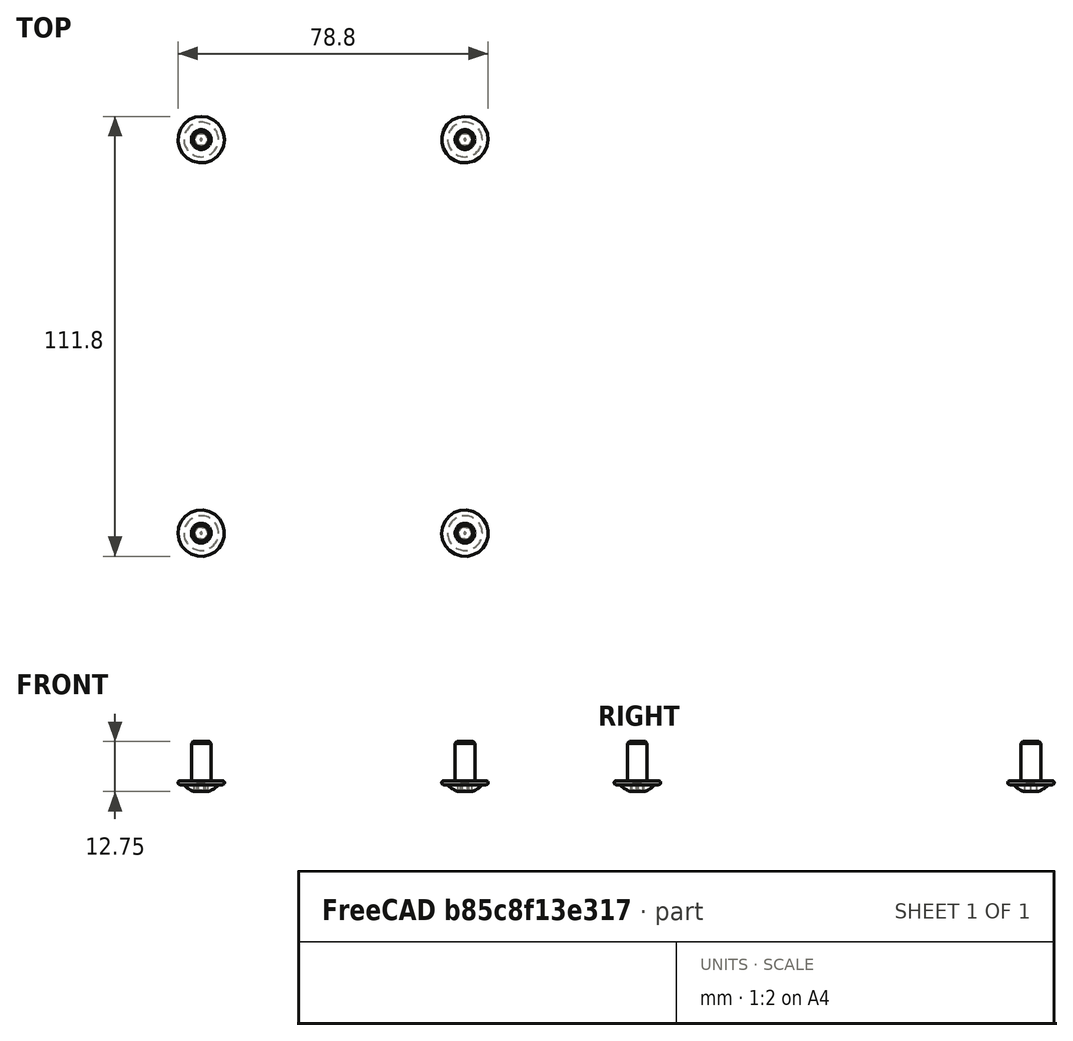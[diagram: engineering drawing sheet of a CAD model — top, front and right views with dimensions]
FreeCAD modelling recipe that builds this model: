
FCSTD DOCUMENT  (FreeCAD 1.0R39319 (Git))
Label: Assy_Stack_Module
License: All rights reserved
LicenseURL: https://en.wikipedia.org/wiki/All_rights_reserved
objects: App::Link×5, Part::FeaturePython×4, App::DocumentObjectGroup×3, PartDesign::CoordinateSystem×1, App::FeaturePython×1, App::Part×1
note: 5 computed .brp shape members not serialized (recipe doc carries the construction recipe); baked Part::Feature solids carry a one-line shape summary decoded from their .brp
EXTERNAL_REF file=../../Part/Print/Stack_Module.FCStd obj=screen_ref
EXTERNAL_REF file=../../Part/Print/Stack_Module.FCStd obj=Part
EXTERNAL_REF file=../../Part/Print/Spacer.FCStd obj=LCS_1
EXTERNAL_REF file=../../Part/Print/Stack_Module.FCStd obj=spacer_att_1
EXTERNAL_REF file=../../Part/Print/Spacer.FCStd obj=Part
EXTERNAL_REF file=../../Part/Print/Stack_Module.FCStd obj=spacer_att_2
EXTERNAL_REF file=../../Part/Print/Stack_Module.FCStd obj=spacer_att_3
EXTERNAL_REF file=../../Part/Print/Stack_Module.FCStd obj=spacer_att_4

FEATURE [App::DocumentObjectGroup] Parts
FEATURE [PartDesign::CoordinateSystem] LCS_Origin
  AttacherType = Attacher::AttachEngine3D
  AttachmentSupport = -> [X_Axis]
  MapMode = 2
FEATURE [App::DocumentObjectGroup] Constraints
FEATURE [App::FeaturePython] Variables  # WARN: FeaturePython — macro-defined, semantics opaque (R4)
  Type = App::PropertyContainer
FEATURE [App::DocumentObjectGroup] Configurations
FEATURE [App::Link] Stack_Module
  AttachedBy = #screen_ref
  AttachedTo = Parent Assembly#LCS_Origin
  LinkPlacement = pos=(19.9856,50,3) rot=(0.57735,0.57735,0.57735;2.0944rad)
  LinkedObject = -> <external ../../Part/Print/Stack_Module.FCStd>#Part
  Placement = pos=(19.9856,50,3) rot=(0.57735,0.57735,0.57735;2.0944rad)
  SolverId = Asm4EE
  expr: Placement = LCS_Origin.Placement * AttachmentOffset * Stack_Module#screen_ref.Placement ^ -1
FEATURE [App::Link] Spacer
  AttachedBy = #LCS_1
  AttachedTo = Stack_Module#spacer_att_1
  LinkPlacement = pos=(-33.5144,116.5,-79.5) rot=(0.707107,0.707107,0;3.14159rad)
  LinkedObject = -> <external ../../Part/Print/Spacer.FCStd>#Part
  Placement = pos=(-33.5144,116.5,-79.5) rot=(0.707107,0.707107,0;3.14159rad)
  SolverId = Asm4EE
  expr: Placement = Stack_Module.Placement * Stack_Module#spacer_att_1.Placement * AttachmentOffset * Spacer#LCS_1.Placement ^ -1
FEATURE [App::Link] Spacer001
  AttachedBy = #LCS_1
  AttachedTo = Stack_Module#spacer_att_2
  LinkPlacement = pos=(82.4856,113.5,-79.5) rot=(0.707107,0.707107,0;3.14159rad)
  LinkedObject = -> <external ../../Part/Print/Spacer.FCStd>#Part
  Placement = pos=(82.4856,113.5,-79.5) rot=(0.707107,0.707107,0;3.14159rad)
  SolverId = Asm4EE
  expr: Placement = Stack_Module.Placement * Stack_Module#spacer_att_2.Placement * AttachmentOffset * Spacer#LCS_1.Placement ^ -1
FEATURE [App::Link] Spacer002
  AttachedBy = #LCS_1
  AttachedTo = Stack_Module#spacer_att_3
  AttachmentOffset = pos=(0,0,0) rot=(0,1,0;3.14159rad)
  LinkPlacement = pos=(-33.5144,-16.5,-79.5) rot=(0.707107,-0.707107,0;3.14159rad)
  LinkedObject = -> <external ../../Part/Print/Spacer.FCStd>#Part
  Placement = pos=(-33.5144,-16.5,-79.5) rot=(0.707107,-0.707107,0;3.14159rad)
  SolverId = Asm4EE
  expr: Placement = Stack_Module.Placement * Stack_Module#spacer_att_3.Placement * AttachmentOffset * Spacer#LCS_1.Placement ^ -1
FEATURE [App::Link] Spacer003
  AttachedBy = #LCS_1
  AttachedTo = Stack_Module#spacer_att_4
  AttachmentOffset = pos=(0,0,0) rot=(0,1,0;3.14159rad)
  LinkPlacement = pos=(82.4856,-13.5,-79.5) rot=(0.707107,-0.707107,0;3.14159rad)
  LinkedObject = -> <external ../../Part/Print/Spacer.FCStd>#Part
  Placement = pos=(82.4856,-13.5,-79.5) rot=(0.707107,-0.707107,0;3.14159rad)
  SolverId = Asm4EE
  expr: Placement = Stack_Module.Placement * Stack_Module#spacer_att_4.Placement * AttachmentOffset * Spacer#LCS_1.Placement ^ -1
FEATURE [Part::FeaturePython] Screw  label="M5x10-Screw"  # WARN: FeaturePython — macro-defined, semantics opaque (R4)
  BaseObject = -> Stack_Module [Body.Mirrored.Edge531]
  Diameter = 3
  Invert = true
  LeftHanded = false
  Length = 1
  LengthCustom = 10
  MatchOuter = false
  OffsetAngle = 0
  Placement = pos=(-31.0144,2.23e-14,-3) rot=(0.830469,-0.557065,0;3.14159rad)
  Thread = false
  Type = 86
FEATURE [Part::FeaturePython] Screw001  label="M5x10-Screw007"  # WARN: FeaturePython — macro-defined, semantics opaque (R4)
  BaseObject = -> Stack_Module [Body.Mirrored.Edge537]
  Diameter = 3
  Invert = true
  LeftHanded = false
  Length = 1
  LengthCustom = 10
  MatchOuter = false
  OffsetAngle = 0
  Placement = pos=(35.9856,8.1e-15,-3) rot=(0.830469,-0.557065,0;3.14159rad)
  Thread = false
  Type = 86
FEATURE [Part::FeaturePython] Screw002  label="M5x10-Screw008"  # WARN: FeaturePython — macro-defined, semantics opaque (R4)
  BaseObject = -> Stack_Module [Body.Mirrored.Edge265]
  Diameter = 3
  Invert = false
  LeftHanded = false
  Length = 1
  LengthCustom = 10
  MatchOuter = false
  OffsetAngle = 0
  Placement = pos=(35.9856,100,-3) rot=(-1,0,0;3.14159rad)
  Thread = false
  Type = 86
FEATURE [Part::FeaturePython] Screw003  label="M5x10-Screw009"  # WARN: FeaturePython — macro-defined, semantics opaque (R4)
  BaseObject = -> Stack_Module [Body.Mirrored.Edge258]
  Diameter = 3
  Invert = false
  LeftHanded = false
  Length = 1
  LengthCustom = 10
  MatchOuter = false
  OffsetAngle = 0
  Placement = pos=(-31.0144,100,-3) rot=(-1,0,0;3.14159rad)
  Thread = false
  Type = 86
FEATURE [App::Part] Assembly  label="Assy_Stack_Module"
  AssemblyType = Part::Link
  Group = -> [LCS_Origin,Constraints,Variables,Configurations,Stack_Module,Spacer,Spacer001,Spacer002,Spacer003,Screw,Screw001,Screw002,Screw003]
  Origin = -> Origin
  Type = Assembly

RESOLVED EXTERNAL PARTS (link-assembly join: the EXTERNAL_REF files above that resolve inside this repo's crawl, each included once):
---- part ../../Part/Print/Spacer.FCStd = doc fcstd_2f39e15fa6d1 ----
FCSTD DOCUMENT  (FreeCAD 1.0R39319 (Git))
Label: Spacer
License: All rights reserved
LicenseURL: https://en.wikipedia.org/wiki/All_rights_reserved
objects: Sketcher::SketchObject×1, PartDesign::Pad×1, PartDesign::Chamfer×1, PartDesign::Body×1, PartDesign::CoordinateSystem×1, App::Part×1
note: 10 computed .brp shape members not serialized (recipe doc carries the construction recipe); baked Part::Feature solids carry a one-line shape summary decoded from their .brp

FEATURE [Sketcher::SketchObject] Sketch
  ArcFitTolerance = 1e-06
  AttachmentSupport = -> [XY_Plane001]
  FullyConstrained = true
  MakeInternals = false
  MapMode = 5
  sketch-geometry (2):
    g0: Circle CenterX=0 CenterY=0 CenterZ=0 NormalX=0 NormalY=0 NormalZ=1 AngleXU=0 Radius=4.25
    g1: Circle CenterX=0 CenterY=0 CenterZ=0 NormalX=0 NormalY=0 NormalZ=1 AngleXU=0 Radius=3.25
  constraints (4):
    c: Coincident(g0,g-1)
    c: Coincident(g1,g0)
    c: Diameter(g1) = 6.5
    c: Diameter(g0) = 8.5
FEATURE [PartDesign::Pad] Pad
  Direction = (0,0,1)
  Length = 7
  Length2 = 10
  Profile = -> Sketch
  ReferenceAxis = -> Sketch [N_Axis]
  Refine = true
  Suppressed = false
  Type = 0
FEATURE [PartDesign::Chamfer] Chamfer
  Angle = 45
  Base = -> Pad [Edge3,Edge2]
  BaseFeature = -> Pad
  ChamferType = 0
  FlipDirection = false
  Refine = true
  Size = 0.25
  Size2 = 1
  SupportTransform = false
  Suppressed = false
  UseAllEdges = false
FEATURE [PartDesign::Body] Body  label="Spacer001"
  AllowCompound = false
  Group = -> [Sketch,Pad,Chamfer]
  Origin = -> Origin001
  Tip = -> Chamfer
FEATURE [PartDesign::CoordinateSystem] LCS_1
  AttacherType = Attacher::AttachEngine3D
  AttachmentSupport = -> [Chamfer]
  MapMode = 11
  Placement = pos=(0,0,0) rot=(0,0,1;1.5708rad)
FEATURE [App::Part] Part  label="Spacer"
  Group = -> [Body,LCS_1]
  Origin = -> Origin
---- part ../../Part/Print/Stack_Module.FCStd = doc fcstd_a0bce2ddf035 ----
FCSTD DOCUMENT  (FreeCAD 1.0R39319 (Git))
Label: Stack_Module
License: All rights reserved
LicenseURL: https://en.wikipedia.org/wiki/All_rights_reserved
objects: Sketcher::SketchObject×20, PartDesign::Pocket×15, PartDesign::CoordinateSystem×7, PartDesign::Pad×6, PartDesign::Fillet×5, PartDesign::LinearPattern×2, PartDesign::Mirrored×1, PartDesign::Body×1, App::Part×1
note: 132 computed .brp shape members not serialized (recipe doc carries the construction recipe); baked Part::Feature solids carry a one-line shape summary decoded from their .brp

FEATURE [Sketcher::SketchObject] Sketch
  ArcFitTolerance = 1e-06
  AttachmentSupport = -> [XZ_Plane001]
  FullyConstrained = true
  MakeInternals = false
  MapMode = 5
  Placement = pos=(0,0,0) rot=(1,0,0;1.5708rad)
  sketch-geometry (9):
    g0: LineSegment StartX=0 StartY=-70 StartZ=0 EndX=74 EndY=-70 EndZ=0
    g1: LineSegment StartX=74 StartY=-70 StartZ=0 EndX=74 EndY=-53.5 EndZ=0
    g2: ArcOfCircle CenterX=66.5 CenterY=-53.5 CenterZ=0 NormalX=0 NormalY=0 NormalZ=1 AngleXU=0 Radius=7.5 StartAngle=0 EndAngle=1.5708
    g3: ArcOfCircle CenterX=66.5 CenterY=-38.5 CenterZ=0 NormalX=0 NormalY=0 NormalZ=1 AngleXU=0 Radius=7.5 StartAngle=3.14159 EndAngle=4.71239
    g4: LineSegment StartX=59 StartY=-38.5 StartZ=0 EndX=59 EndY=47.8031 EndZ=0
    g5: ArcOfCircle CenterX=66.5 CenterY=47.8031 CenterZ=0 NormalX=0 NormalY=0 NormalZ=1 AngleXU=0 Radius=7.5 StartAngle=1.77215 EndAngle=3.14159
    g6: ArcOfCircle CenterX=63.5 CenterY=62.5 CenterZ=0 NormalX=0 NormalY=0 NormalZ=1 AngleXU=0 Radius=7.5 StartAngle=4.91375 EndAngle=7.85398
    g7: LineSegment StartX=63.5 StartY=70 StartZ=0 EndX=0 EndY=70 EndZ=0
    g8: LineSegment StartX=0 StartY=70 StartZ=0 EndX=0 EndY=-70 EndZ=0
  constraints (26):
    c: PointOnObject(g0,g-2)
    c: Horizontal(g0)
    c: Coincident(g0,g1)
    c: Vertical(g1)
    c: Tangent(g1,g2) = -1.5708
    c: Tangent(g2,g3) = 1.5708
    c: Tangent(g3,g4) = 1.5708
    c: Tangent(g4,g5) = 1.5708
    c: Tangent(g5,g6) = 1.5708
    c: Tangent(g6,g7) = -1.5708
    c: Coincident(g7,g8)
    c: Coincident(g8,g0)
    c: Vertical(g8)
    c: Horizontal(g7)
    c: Vertical(g4)
    c: DistanceX(g0,g0) = 74
    c: Distance(g7,g0) = 140
    c: Distance(g2,g0) = 16.5
    c: Radius(g2) = 7.5
    c: Distance(g8,g4) = 59
    c: Radius(g6) = 7.5
    c: Distance(g6,g8) = 63.5
    c: Distance(g2,g8) = 66.5
    c: Distance(g-1,g0) = 70
    c: Radius(g3) = 7.5
    c: Radius(g5) = 7.5
FEATURE [PartDesign::Pad] Pad
  Direction = (0,-1,2e-16)
  Length = 87.5
  Length2 = 10
  Placement = pos=(0,0,0) rot=(1,0,0;1.5708rad)
  Profile = -> Sketch
  ReferenceAxis = -> Sketch [N_Axis]
  Refine = true
  Suppressed = false
  Type = 0
FEATURE [Sketcher::SketchObject] Sketch001
  ArcFitTolerance = 1e-06
  AttachmentSupport = -> [Pad]
  ExternalGeometry = -> [Pad]
  FullyConstrained = true
  MakeInternals = false
  MapMode = 5
  Placement = pos=(0,-87.5,0) rot=(1,0,0;1.5708rad)
  sketch-geometry (6):
    g0: LineSegment StartX=0 StartY=-60 StartZ=0 EndX=0 EndY=-70 EndZ=0
    g1: LineSegment StartX=70 StartY=-67 StartZ=0 EndX=70 EndY=-60 EndZ=0
    g2: LineSegment StartX=70 StartY=-60 StartZ=0 EndX=0 EndY=-60 EndZ=0
    g3: LineSegment StartX=70 StartY=-67 StartZ=0 EndX=65 EndY=-67 EndZ=0
    g4: LineSegment StartX=65 StartY=-67 StartZ=0 EndX=65 EndY=-70 EndZ=0
    g5: LineSegment StartX=65 StartY=-70 StartZ=0 EndX=0 EndY=-70 EndZ=0
  constraints (17):
    c: Coincident(g1,g2)
    c: Coincident(g2,g0)
    c: Vertical(g0)
    c: Vertical(g1)
    c: Horizontal(g2)
    c: Distance(g-2,g1) = 70
    c: Coincident(g1,g3)
    c: Horizontal(g3)
    c: Coincident(g3,g4)
    c: PointOnObject(g4,g-3)
    c: Coincident(g4,g5)
    c: Coincident(g5,g-3)
    c: Coincident(g0,g5)
    c: Vertical(g4)
    c: Distance(g3,g2) = 7
    c: Distance(g5,g3) = 3
    c: Distance(g-2,g4) = 65
FEATURE [PartDesign::Pocket] Pocket
  BaseFeature = -> Pad
  Direction = (0,1,-2e-16)
  Length = 5
  Length2 = 5
  Placement = pos=(0,0,0) rot=(1,0,0;1.5708rad)
  Profile = -> Sketch001
  ReferenceAxis = -> Sketch001 [N_Axis]
  Refine = true
  Suppressed = false
  Type = 1
FEATURE [Sketcher::SketchObject] Sketch002
  ArcFitTolerance = 1e-06
  AttachmentSupport = -> [Pocket]
  ExternalGeometry = -> [Pocket]
  FullyConstrained = true
  MakeInternals = false
  MapMode = 5
  Placement = pos=(0,-87.5,0) rot=(1,0,0;1.5708rad)
  sketch-geometry (4):
    g0: LineSegment StartX=0 StartY=28 StartZ=0 EndX=0 EndY=-60 EndZ=0
    g1: LineSegment StartX=0 StartY=-60 StartZ=0 EndX=56 EndY=-60 EndZ=0
    g2: LineSegment StartX=56 StartY=-60 StartZ=0 EndX=56 EndY=28 EndZ=0
    g3: LineSegment StartX=56 StartY=28 StartZ=0 EndX=0 EndY=28 EndZ=0
  constraints (12):
    c: Coincident(g0,g1)
    c: Coincident(g1,g2)
    c: Coincident(g2,g3)
    c: Coincident(g3,g0)
    c: Vertical(g0)
    c: Vertical(g2)
    c: Horizontal(g1)
    c: Horizontal(g3)
    c: PointOnObject(g0,g-2)
    c: PointOnObject(g1,g-3)
    c: Distance(g-4,g2) = 3
    c: Distance(g3,g1) = 88
FEATURE [PartDesign::Pocket] Pocket001
  BaseFeature = -> Pocket
  Direction = (0,1,-2e-16)
  Length = 0
  Length2 = 5
  Offset = -3
  Placement = pos=(0,0,0) rot=(1,0,0;1.5708rad)
  Profile = -> Sketch002
  ReferenceAxis = -> Sketch002 [N_Axis]
  Refine = true
  Suppressed = false
  Type = 3
  UpToFace = -> Pocket [Face2]
FEATURE [Sketcher::SketchObject] Sketch003
  ArcFitTolerance = 1e-06
  AttachmentSupport = -> [Pocket001]
  ExternalGeometry = -> [Pocket001]
  FullyConstrained = true
  MakeInternals = false
  MapMode = 5
  Placement = pos=(0,-87.5,0) rot=(1,0,0;1.5708rad)
  sketch-geometry (4):
    g0: LineSegment StartX=0 StartY=70 StartZ=0 EndX=0 EndY=25 EndZ=0
    g1: LineSegment StartX=0 StartY=25 StartZ=0 EndX=51 EndY=25 EndZ=0
    g2: LineSegment StartX=51 StartY=25 StartZ=0 EndX=51 EndY=70 EndZ=0
    g3: LineSegment StartX=51 StartY=70 StartZ=0 EndX=0 EndY=70 EndZ=0
  constraints (11):
    c: Coincident(g0,g1)
    c: Coincident(g1,g2)
    c: Coincident(g2,g3)
    c: Coincident(g3,g0)
    c: Vertical(g0)
    c: Vertical(g2)
    c: Horizontal(g1)
    c: Horizontal(g3)
    c: Coincident(g0,g-4)
    c: Distance(g2,g-3) = 5
    c: Distance(g1,g3) = 45
FEATURE [PartDesign::Pocket] Pocket002
  BaseFeature = -> Pocket001
  Direction = (0,1,-2e-16)
  Length = 5
  Length2 = 5
  Placement = pos=(0,0,0) rot=(1,0,0;1.5708rad)
  Profile = -> Sketch003
  ReferenceAxis = -> Sketch003 [N_Axis]
  Refine = true
  Suppressed = false
  Type = 1
FEATURE [PartDesign::Pocket] Pocket003
  BaseFeature = -> Pocket002
  Direction = (0,1,-2e-16)
  Length = 5
  Length2 = 5
  Placement = pos=(0,0,0) rot=(1,0,0;1.5708rad)
  Profile = -> Sketch003
  ReferenceAxis = -> Sketch003 [N_Axis]
  Refine = true
  Suppressed = false
  Type = 1
FEATURE [Sketcher::SketchObject] Sketch004
  ArcFitTolerance = 1e-06
  AttachmentSupport = -> [Pocket003]
  ExternalGeometry = -> [Pocket003]
  FullyConstrained = true
  MakeInternals = false
  MapMode = 5
  Placement = pos=(0,-87.5,0) rot=(1,0,0;1.5708rad)
  sketch-geometry (4):
    g0: LineSegment StartX=51 StartY=67 StartZ=0 EndX=51 EndY=63.5 EndZ=0
    g1: LineSegment StartX=51 StartY=63.5 StartZ=0 EndX=56 EndY=63.5 EndZ=0
    g2: LineSegment StartX=56 StartY=63.5 StartZ=0 EndX=56 EndY=67 EndZ=0
    g3: LineSegment StartX=56 StartY=67 StartZ=0 EndX=51 EndY=67 EndZ=0
  constraints (12):
    c: Coincident(g0,g1)
    c: Coincident(g1,g2)
    c: Coincident(g2,g3)
    c: Coincident(g3,g0)
    c: Vertical(g0)
    c: Vertical(g2)
    c: Horizontal(g1)
    c: Horizontal(g3)
    c: PointOnObject(g0,g-4)
    c: Distance(g-3,g3) = 3
    c: Distance(g3,g1) = 3.5
    c: PointOnObject(g1,g-5)
FEATURE [PartDesign::Pocket] Pocket004
  BaseFeature = -> Pocket003
  Direction = (0,1,-2e-16)
  Length = 5
  Length2 = 5
  Placement = pos=(0,0,0) rot=(1,0,0;1.5708rad)
  Profile = -> Sketch004
  ReferenceAxis = -> Sketch004 [N_Axis]
  Refine = true
  Suppressed = false
  Type = 1
FEATURE [PartDesign::LinearPattern] LinearPattern
  BaseFeature = -> Pocket004
  Direction = -> Z_Axis001
  Length = 32.5
  Mode = 1
  Occurrences = 6
  Offset = 6.5
  Originals = -> [Pocket004]
  Placement = pos=(0,0,0) rot=(1,0,0;1.5708rad)
  Refine = true
  Reversed = true
  Suppressed = false
  TransformMode = 0
FEATURE [Sketcher::SketchObject] Sketch005
  ArcFitTolerance = 1e-06
  AttachmentSupport = -> [LinearPattern]
  ExternalGeometry = -> [LinearPattern]
  FullyConstrained = true
  MakeInternals = false
  MapMode = 5
  Placement = pos=(0,1.1e-14,25) rot=(0,0,1;3.14159rad)
  sketch-geometry (4):
    g0: LineSegment StartX=0 StartY=3 StartZ=0 EndX=-56 EndY=3 EndZ=0
    g1: LineSegment StartX=-56 StartY=3 StartZ=0 EndX=-56 EndY=33 EndZ=0
    g2: LineSegment StartX=0 StartY=3 StartZ=0 EndX=-1.42e-14 EndY=9 EndZ=0
    g3: ArcOfCircle CenterX=0 CenterY=86.3333 CenterZ=0 NormalX=0 NormalY=0 NormalZ=1 AngleXU=0 Radius=77.3333 StartAngle=3.90261 EndAngle=4.71239
  constraints (13):
    c: PointOnObject(g0,g-2)
    c: Horizontal(g0)
    c: Coincident(g0,g1)
    c: Vertical(g1)
    c: Coincident(g2,g0)
    c: PointOnObject(g2,g-2)
    c: Coincident(g3,g2)
    c: Coincident(g3,g1)
    c: PointOnObject(g3,g-2)
    c: DistanceY(g2,g2) = 6
    c: DistanceY(g1,g1) = 30
    c: PointOnObject(g0,g-3)
    c: PointOnObject(g1,g-4)
FEATURE [PartDesign::Pad] Pad001
  BaseFeature = -> LinearPattern
  Direction = (0,0,1)
  Length = 3
  Length2 = 10
  Placement = pos=(0,0,0) rot=(1,0,0;1.5708rad)
  Profile = -> Sketch005
  ReferenceAxis = -> Sketch005 [N_Axis]
  Refine = true
  Reversed = true
  Suppressed = false
  Type = 0
FEATURE [Sketcher::SketchObject] Sketch006
  ArcFitTolerance = 1e-06
  AttachmentSupport = -> [Pad001]
  ExternalGeometry = -> [Pad001]
  FullyConstrained = true
  MakeInternals = false
  MapMode = 5
  Placement = pos=(0,-3,7e-16) rot=(1,0,0;1.5708rad)
  sketch-geometry (8):
    g0: LineSegment StartX=56 StartY=22 StartZ=0 EndX=44 EndY=22 EndZ=0
    g1: LineSegment StartX=44 StartY=22 StartZ=0 EndX=44 EndY=10 EndZ=0
    g2: LineSegment StartX=44 StartY=10 StartZ=0 EndX=56 EndY=10 EndZ=0
    g3: LineSegment StartX=56 StartY=10 StartZ=0 EndX=56 EndY=22 EndZ=0
    g4: LineSegment StartX=56 StartY=-45 StartZ=0 EndX=44 EndY=-45 EndZ=0
    g5: LineSegment StartX=44 StartY=-45 StartZ=0 EndX=44 EndY=-57 EndZ=0
    g6: LineSegment StartX=44 StartY=-57 StartZ=0 EndX=56 EndY=-57 EndZ=0
    g7: LineSegment StartX=56 StartY=-57 StartZ=0 EndX=56 EndY=-45 EndZ=0
  constraints (23):
    c: Coincident(g0,g1)
    c: Coincident(g1,g2)
    c: Coincident(g2,g3)
    c: Coincident(g3,g0)
    c: Horizontal(g0)
    c: Horizontal(g2)
    c: Vertical(g1)
    c: Vertical(g3)
    c: Coincident(g4,g5)
    c: Coincident(g5,g6)
    c: Coincident(g6,g7)
    c: Coincident(g7,g4)
    c: Horizontal(g4)
    c: Horizontal(g6)
    c: Vertical(g5)
    c: Vertical(g7)
    c: DistanceX(g0,g0) = 12
    c: Distance(g2,g0) = 12
    c: Distance(g6,g4) = 12
    c: Distance(g7,g5) = 12
    c: Coincident(g0,g-5)
    c: PointOnObject(g4,g-3)
    c: Distance(g-4,g6) = 3
FEATURE [PartDesign::Pad] Pad002
  BaseFeature = -> Pad001
  Direction = (0,-1,2e-16)
  Length = 3
  Length2 = 10
  Placement = pos=(0,0,0) rot=(1,0,0;1.5708rad)
  Profile = -> Sketch006
  ReferenceAxis = -> Sketch006 [N_Axis]
  Refine = true
  Suppressed = false
  Type = 0
FEATURE [PartDesign::Fillet] Fillet
  Base = -> Pad002 [Edge152,Edge151]
  BaseFeature = -> Pad002
  Placement = pos=(0,0,0) rot=(1,0,0;1.5708rad)
  Radius = 6
  Refine = true
  SupportTransform = false
  Suppressed = false
  UseAllEdges = false
FEATURE [Sketcher::SketchObject] Sketch007
  ArcFitTolerance = 1e-06
  AttachmentSupport = -> [Fillet]
  ExternalGeometry = -> [Fillet]
  FullyConstrained = true
  MakeInternals = false
  MapMode = 5
  Placement = pos=(0,-87.5,0) rot=(1,0,0;1.5708rad)
  sketch-geometry (8):
    g0: LineSegment StartX=56 StartY=22 StartZ=0 EndX=56 EndY=10 EndZ=0
    g1: LineSegment StartX=56 StartY=10 StartZ=0 EndX=50 EndY=10 EndZ=0
    g2: ArcOfCircle CenterX=50 CenterY=16 CenterZ=0 NormalX=0 NormalY=0 NormalZ=1 AngleXU=0 Radius=6 StartAngle=1.5708 EndAngle=4.71239
    g3: LineSegment StartX=50 StartY=22 StartZ=0 EndX=56 EndY=22 EndZ=0
    g4: LineSegment StartX=56 StartY=-57 StartZ=0 EndX=56 EndY=-45 EndZ=0
    g5: LineSegment StartX=56 StartY=-45 StartZ=0 EndX=44 EndY=-45 EndZ=0
    g6: LineSegment StartX=44 StartY=-45 StartZ=0 EndX=44 EndY=-57 EndZ=0
    g7: LineSegment StartX=44 StartY=-57 StartZ=0 EndX=56 EndY=-57 EndZ=0
  constraints (17):
    c: Coincident(g0,g1)
    c: Horizontal(g1)
    c: Tangent(g1,g2) = 1.5708
    c: Tangent(g2,g3) = 1.5708
    c: Coincident(g3,g0)
    c: Coincident(g0,g-3)
    c: Coincident(g0,g-5)
    c: Coincident(g-6,g2)
    c: Coincident(g4,g5)
    c: Coincident(g5,g6)
    c: Coincident(g6,g7)
    c: Coincident(g7,g4)
    c: Vertical(g6)
    c: Horizontal(g5)
    c: Coincident(g-9,g4)
    c: Coincident(g6,g-8)
    c: Coincident(g4,g-7)
FEATURE [PartDesign::Pad] Pad003
  BaseFeature = -> Fillet
  Direction = (0,-1,2e-16)
  Length = 25
  Length2 = 10
  Placement = pos=(0,0,0) rot=(1,0,0;1.5708rad)
  Profile = -> Sketch007
  ReferenceAxis = -> Sketch007 [N_Axis]
  Refine = true
  Reversed = true
  Suppressed = false
  Type = 0
FEATURE [Sketcher::SketchObject] Sketch008
  ArcFitTolerance = 1e-06
  AttachmentSupport = -> [Pad003]
  ExternalGeometry = -> [Pad003]
  FullyConstrained = true
  MakeInternals = false
  MapMode = 5
  Placement = pos=(0,-2.64e-14,-60) rot=(1,0,0;3.14159rad)
  sketch-geometry (7):
    g0: LineSegment StartX=56 StartY=87.5 StartZ=0 EndX=44 EndY=87.5 EndZ=0
    g1: LineSegment StartX=44 StartY=87.5 StartZ=0 EndX=44 EndY=84.5 EndZ=0
    g2: LineSegment StartX=44 StartY=84.5 StartZ=0 EndX=56 EndY=63.7154 EndZ=0
    g3: LineSegment StartX=56 StartY=63.7154 StartZ=0 EndX=56 EndY=87.5 EndZ=0
    g4: LineSegment StartX=56 StartY=23.7846 StartZ=0 EndX=44 EndY=3 EndZ=0
    g5: LineSegment StartX=44 StartY=3 StartZ=0 EndX=56 EndY=3 EndZ=0
    g6: LineSegment StartX=56 StartY=3 StartZ=0 EndX=56 EndY=23.7846 EndZ=0
  constraints (18):
    c: Coincident(g-5,g0)
    c: Coincident(g0,g-5)
    c: Coincident(g0,g1)
    c: PointOnObject(g1,g-4)
    c: Coincident(g1,g2)
    c: PointOnObject(g2,g-3)
    c: Coincident(g2,g3)
    c: Coincident(g3,g0)
    c: PointOnObject(g4,g-3)
    c: PointOnObject(g4,g-6)
    c: Coincident(g4,g5)
    c: Coincident(g5,g-6)
    c: Coincident(g5,g6)
    c: Coincident(g6,g4)
    c: Angle(g4,g6) = 0.523599
    c: Angle(g3,g2) = 0.523599
    c: DistanceY(g1,g1) = 3
    c: PointOnObject(g4,g-4)
FEATURE [PartDesign::Pad] Pad004
  BaseFeature = -> Pad003
  Direction = (0,0,-1)
  Length = 10
  Length2 = 10
  Placement = pos=(0,0,0) rot=(1,0,0;1.5708rad)
  Profile = -> Sketch008
  ReferenceAxis = -> Sketch008 [N_Axis]
  Refine = true
  Suppressed = false
  Type = 3
  UpToFace = -> Pad003 [Face14]
FEATURE [Sketcher::SketchObject] Sketch009
  ArcFitTolerance = 1e-06
  AttachmentSupport = -> [Pad004]
  ExternalGeometry = -> [Pad004]
  FullyConstrained = true
  MakeInternals = false
  MapMode = 5
  Placement = pos=(0,-2.51e-14,-57) rot=(1,0,0;3.14159rad)
  sketch-geometry (3):
    g0: LineSegment StartX=44 StartY=3 StartZ=0 EndX=44 EndY=6 EndZ=0
    g1: LineSegment StartX=44 StartY=6 StartZ=0 EndX=45.7321 EndY=6 EndZ=0
    g2: LineSegment StartX=45.7321 StartY=6 StartZ=0 EndX=44 EndY=3 EndZ=0
  constraints (6):
    c: Coincident(g-5,g0)
    c: Coincident(g0,g-4)
    c: Coincident(g0,g1)
    c: Coincident(g1,g-3)
    c: Coincident(g1,g2)
    c: Coincident(g2,g0)
FEATURE [PartDesign::Pocket] Pocket005
  BaseFeature = -> Pad004
  Direction = (0,0,1)
  Length = 0
  Length2 = 5
  Placement = pos=(0,0,0) rot=(1,0,0;1.5708rad)
  Profile = -> Sketch009
  ReferenceAxis = -> Sketch009 [N_Axis]
  Refine = true
  Suppressed = false
  Type = 3
  UpToFace = -> Pad004 [Face3]
FEATURE [Sketcher::SketchObject] Sketch010
  ArcFitTolerance = 1e-06
  AttachmentSupport = -> [Pocket005]
  ExternalGeometry = -> [Pocket005]
  FullyConstrained = true
  MakeInternals = false
  MapMode = 5
  Placement = pos=(0,-2.51e-14,-57) rot=(1,0,0;3.14159rad)
  sketch-geometry (4):
    g0: LineSegment StartX=44 StartY=84.5 StartZ=0 EndX=44 EndY=62.5 EndZ=0
    g1: LineSegment StartX=44 StartY=62.5 StartZ=0 EndX=56 EndY=62.5 EndZ=0
    g2: LineSegment StartX=56 StartY=62.5 StartZ=0 EndX=56 EndY=63.7154 EndZ=0
    g3: LineSegment StartX=56 StartY=63.7154 StartZ=0 EndX=44 EndY=84.5 EndZ=0
  constraints (8):
    c: Coincident(g-6,g0)
    c: Coincident(g0,g-4)
    c: Coincident(g0,g1)
    c: Coincident(g1,g-4)
    c: Coincident(g1,g2)
    c: Coincident(g2,g-6)
    c: Coincident(g2,g3)
    c: Coincident(g3,g0)
FEATURE [PartDesign::Pocket] Pocket006
  BaseFeature = -> Pocket005
  Direction = (0,0,1)
  Length = 0
  Length2 = 5
  Placement = pos=(0,0,0) rot=(1,0,0;1.5708rad)
  Profile = -> Sketch010
  ReferenceAxis = -> Sketch010 [N_Axis]
  Refine = true
  Suppressed = false
  Type = 3
  UpToFace = -> Pocket005 [Face19]
FEATURE [PartDesign::Fillet] Fillet001
  Base = -> Pocket006 [Edge105]
  BaseFeature = -> Pocket006
  Placement = pos=(0,0,0) rot=(1,0,0;1.5708rad)
  Radius = 6
  Refine = true
  SupportTransform = false
  Suppressed = false
  UseAllEdges = false
FEATURE [PartDesign::Fillet] Fillet002
  Base = -> Fillet001 [Edge54,Edge52,Edge67,Edge59]
  BaseFeature = -> Fillet001
  Placement = pos=(0,0,0) rot=(1,0,0;1.5708rad)
  Radius = 6
  Refine = true
  SupportTransform = false
  Suppressed = false
  UseAllEdges = false
FEATURE [Sketcher::SketchObject] Sketch011
  ArcFitTolerance = 1e-06
  AttachmentSupport = -> [Fillet002]
  ExternalGeometry = -> [Fillet002]
  FullyConstrained = true
  MakeInternals = false
  MapMode = 5
  Placement = pos=(0,-3,7e-16) rot=(1,0,0;1.5708rad)
  sketch-geometry (4):
    g0: LineSegment StartX=1.42e-14 StartY=22 StartZ=0 EndX=1.42e-14 EndY=10 EndZ=0
    g1: LineSegment StartX=1.42e-14 StartY=10 StartZ=0 EndX=12 EndY=10 EndZ=0
    g2: LineSegment StartX=12 StartY=10 StartZ=0 EndX=12 EndY=22 EndZ=0
    g3: LineSegment StartX=12 StartY=22 StartZ=0 EndX=1.42e-14 EndY=22 EndZ=0
  constraints (11):
    c: Coincident(g0,g1)
    c: Coincident(g1,g2)
    c: Coincident(g2,g3)
    c: Coincident(g3,g0)
    c: Vertical(g0)
    c: Vertical(g2)
    c: Horizontal(g1)
    c: Horizontal(g3)
    c: Coincident(g0,g-3)
    c: Distance(g0,g2) = 12
    c: PointOnObject(g1,g-4)
FEATURE [PartDesign::Pad] Pad005
  BaseFeature = -> Fillet002
  Direction = (0,-1,2e-16)
  Length = 3
  Length2 = 10
  Placement = pos=(0,0,0) rot=(1,0,0;1.5708rad)
  Profile = -> Sketch011
  ReferenceAxis = -> Sketch011 [N_Axis]
  Refine = true
  Suppressed = false
  Type = 0
FEATURE [PartDesign::Fillet] Fillet003
  Base = -> Pad005 [Edge204]
  BaseFeature = -> Pad005
  Placement = pos=(0,0,0) rot=(1,0,0;1.5708rad)
  Radius = 6
  Refine = true
  SupportTransform = false
  Suppressed = false
  UseAllEdges = false
FEATURE [Sketcher::SketchObject] Sketch012
  ArcFitTolerance = 1e-06
  AttachmentSupport = -> [Fillet003]
  ExternalGeometry = -> [Fillet003]
  FullyConstrained = true
  MakeInternals = false
  MapMode = 5
  Placement = pos=(0,-3,7e-16) rot=(1,0,0;1.5708rad)
  sketch-geometry (5):
    g0: ArcOfCircle CenterX=50 CenterY=7 CenterZ=0 NormalX=0 NormalY=0 NormalZ=1 AngleXU=0 Radius=3 StartAngle=2e-16 EndAngle=3.14159
    g1: ArcOfCircle CenterX=50 CenterY=-42 CenterZ=0 NormalX=0 NormalY=0 NormalZ=1 AngleXU=0 Radius=3 StartAngle=3.14159 EndAngle=6.28319
    g2: LineSegment StartX=53 StartY=7 StartZ=0 EndX=53 EndY=-42 EndZ=0
    g3: LineSegment StartX=47 StartY=7 StartZ=0 EndX=47 EndY=-42 EndZ=0
    g4: LineSegment [constr] StartX=50 StartY=7 StartZ=0 EndX=50 EndY=-42 EndZ=0
  constraints (12):
    c: Tangent(g0,g2) = 1.5708
    c: Tangent(g0,g3) = -1.5708
    c: Tangent(g1,g2) = 1.5708
    c: Tangent(g1,g3) = -1.5708
    c: Equal(g0,g1)
    c: Vertical(g3)
    c: Distance(g2,g3) = 6
    c: Coincident(g4,g0)
    c: Coincident(g4,g1)
    c: PointOnObject(g-3,g4)
    c: Tangent(g0,g-5)
    c: Tangent(g1,g-6)
FEATURE [PartDesign::Pocket] Pocket007
  BaseFeature = -> Fillet003
  Direction = (0,1,-2e-16)
  Length = 5
  Length2 = 5
  Placement = pos=(0,0,0) rot=(1,0,0;1.5708rad)
  Profile = -> Sketch012
  ReferenceAxis = -> Sketch012 [N_Axis]
  Refine = true
  Suppressed = false
  Type = 1
FEATURE [Sketcher::SketchObject] Sketch013
  ArcFitTolerance = 1e-06
  AttachmentSupport = -> [Pocket007]
  ExternalGeometry = -> [Pocket007]
  FullyConstrained = true
  MakeInternals = false
  MapMode = 5
  Placement = pos=(0,-3,7e-16) rot=(1,0,0;1.5708rad)
  sketch-geometry (4):
    g0: ArcOfCircle CenterX=0 CenterY=4 CenterZ=0 NormalX=0 NormalY=0 NormalZ=1 AngleXU=0 Radius=3 StartAngle=7.15e-14 EndAngle=3.14159
    g1: ArcOfCircle CenterX=1.8053e-12 CenterY=-36 CenterZ=0 NormalX=0 NormalY=0 NormalZ=1 AngleXU=0 Radius=3 StartAngle=3.14159 EndAngle=6.28319
    g2: LineSegment StartX=3 StartY=4 StartZ=0 EndX=3 EndY=-36 EndZ=0
    g3: LineSegment StartX=-3 StartY=4 StartZ=0 EndX=-3 EndY=-36 EndZ=0
  constraints (10):
    c: Tangent(g0,g2) = 1.5708
    c: Tangent(g0,g3) = -1.5708
    c: Tangent(g1,g2) = 1.5708
    c: Tangent(g1,g3) = -1.5708
    c: Equal(g0,g1)
    c: Vertical(g3)
    c: PointOnObject(g0,g-2)
    c: Distance(g2,g3) = 6
    c: Distance(g0,g-3) = 21
    c: Distance(g1,g-4) = 24
FEATURE [PartDesign::Pocket] Pocket008
  BaseFeature = -> Pocket007
  Direction = (0,1,-2e-16)
  Length = 5
  Length2 = 5
  Placement = pos=(0,0,0) rot=(1,0,0;1.5708rad)
  Profile = -> Sketch013
  ReferenceAxis = -> Sketch013 [N_Axis]
  Refine = true
  Suppressed = false
  Type = 0
FEATURE [Sketcher::SketchObject] Sketch014
  ArcFitTolerance = 1e-06
  AttachmentSupport = -> [Pocket008]
  ExternalGeometry = -> [Pocket008]
  FullyConstrained = true
  MakeInternals = false
  MapMode = 5
  Placement = pos=(0,-3,7e-16) rot=(1,0,0;1.5708rad)
  sketch-geometry (4):
    g0: ArcOfCircle CenterX=15 CenterY=13 CenterZ=0 NormalX=0 NormalY=0 NormalZ=1 AngleXU=0 Radius=3 StartAngle=1.5708 EndAngle=4.71239
    g1: ArcOfCircle CenterX=38 CenterY=13 CenterZ=0 NormalX=0 NormalY=0 NormalZ=1 AngleXU=0 Radius=3 StartAngle=4.71239 EndAngle=7.85398
    g2: LineSegment StartX=15 StartY=16 StartZ=0 EndX=38 EndY=16 EndZ=0
    g3: LineSegment StartX=15 StartY=10 StartZ=0 EndX=38 EndY=10 EndZ=0
  constraints (10):
    c: Tangent(g0,g2) = 1.5708
    c: Tangent(g0,g3) = -1.5708
    c: Tangent(g1,g2) = 1.5708
    c: Tangent(g1,g3) = -1.5708
    c: Equal(g0,g1)
    c: Horizontal(g3)
    c: Distance(g3,g2) = 6
    c: Distance(g-5,g2) = 9
    c: Distance(g0,g-3) = 9
    c: Distance(g1,g-4) = 6
FEATURE [PartDesign::Pocket] Pocket009
  BaseFeature = -> Pocket008
  Direction = (0,1,-2e-16)
  Length = 5
  Length2 = 5
  Placement = pos=(0,0,0) rot=(1,0,0;1.5708rad)
  Profile = -> Sketch014
  ReferenceAxis = -> Sketch014 [N_Axis]
  Refine = true
  Suppressed = false
  Type = 1
FEATURE [PartDesign::LinearPattern] LinearPattern001
  BaseFeature = -> Pocket009
  Direction = -> Z_Axis001
  Length = 36
  Mode = 1
  Occurrences = 4
  Offset = 12
  Originals = -> [Pocket009]
  Placement = pos=(0,0,0) rot=(1,0,0;1.5708rad)
  Refine = true
  Reversed = true
  Suppressed = false
  TransformMode = 0
FEATURE [Sketcher::SketchObject] Sketch015
  ArcFitTolerance = 1e-06
  AttachmentSupport = -> [LinearPattern001]
  ExternalGeometry = -> [LinearPattern001]
  FullyConstrained = true
  MakeInternals = false
  MapMode = 5
  Placement = pos=(0,-6,1.4e-15) rot=(1,0,0;1.5708rad)
  sketch-geometry (3):
    g0: Circle CenterX=6 CenterY=16 CenterZ=0 NormalX=0 NormalY=0 NormalZ=1 AngleXU=0 Radius=3
    g1: Circle CenterX=50 CenterY=16 CenterZ=0 NormalX=0 NormalY=0 NormalZ=1 AngleXU=0 Radius=3
    g2: Circle CenterX=50 CenterY=-51 CenterZ=0 NormalX=0 NormalY=0 NormalZ=1 AngleXU=0 Radius=3
  constraints (6):
    c: Coincident(g0,g-3)
    c: Coincident(g1,g-4)
    c: Coincident(g2,g-5)
    c: Diameter(g0) = 6
    c: Diameter(g1) = 6
    c: Diameter(g2) = 6
FEATURE [PartDesign::Pocket] Pocket010
  BaseFeature = -> LinearPattern001
  Direction = (0,1,-2e-16)
  Length = 5
  Length2 = 5
  Placement = pos=(0,0,0) rot=(1,0,0;1.5708rad)
  Profile = -> Sketch015
  ReferenceAxis = -> Sketch015 [N_Axis]
  Refine = true
  Suppressed = false
  Type = 1
FEATURE [Sketcher::SketchObject] Sketch016
  ArcFitTolerance = 1e-06
  AttachmentSupport = -> [Pocket010]
  ExternalGeometry = -> [Pocket010]
  FullyConstrained = true
  MakeInternals = false
  MapMode = 5
  Placement = pos=(0,-87.5,3.76e-14) rot=(1,0,0;1.5708rad)
  sketch-geometry (2):
    g0: Circle CenterX=50 CenterY=16 CenterZ=0 NormalX=0 NormalY=0 NormalZ=1 AngleXU=0 Radius=2.35
    g1: Circle CenterX=50 CenterY=-51 CenterZ=0 NormalX=0 NormalY=0 NormalZ=1 AngleXU=0 Radius=2.35
  constraints (4):
    c: Coincident(g0,g-3)
    c: Coincident(g1,g-4)
    c: Diameter(g0) = 4.7
    c: Diameter(g1) = 4.7
FEATURE [PartDesign::Pocket] Pocket011
  BaseFeature = -> Pocket010
  Direction = (0,1,-2e-16)
  Length = 5
  Length2 = 5
  Placement = pos=(0,0,0) rot=(1,0,0;1.5708rad)
  Profile = -> Sketch016
  ReferenceAxis = -> Sketch016 [N_Axis]
  Refine = true
  Suppressed = false
  Type = 1
FEATURE [PartDesign::Fillet] Fillet004
  Base = -> Pocket011 [Edge263]
  BaseFeature = -> Pocket011
  Placement = pos=(0,0,0) rot=(1,0,0;1.5708rad)
  Radius = 3
  Refine = true
  SupportTransform = false
  Suppressed = false
  UseAllEdges = false
FEATURE [Sketcher::SketchObject] Sketch017
  ArcFitTolerance = 1e-06
  AttachmentSupport = -> [Fillet004]
  ExternalGeometry = -> [Fillet004]
  FullyConstrained = true
  MakeInternals = false
  MapMode = 5
  Placement = pos=(0,-87.5,3.76e-14) rot=(1,0,0;1.5708rad)
  sketch-geometry (2):
    g0: Circle CenterX=63.5 CenterY=62.5 CenterZ=0 NormalX=0 NormalY=0 NormalZ=1 AngleXU=0 Radius=3
    g1: Circle CenterX=66.5 CenterY=-53.5 CenterZ=0 NormalX=0 NormalY=0 NormalZ=1 AngleXU=0 Radius=3
  constraints (4):
    c: Coincident(g0,g-3)
    c: Coincident(g1,g-4)
    c: Diameter(g0) = 6
    c: Diameter(g1) = 6
FEATURE [PartDesign::Pocket] Pocket012
  BaseFeature = -> Fillet004
  Direction = (0,1,-2e-16)
  Length = 5
  Length2 = 5
  Placement = pos=(0,0,0) rot=(1,0,0;1.5708rad)
  Profile = -> Sketch017
  ReferenceAxis = -> Sketch017 [N_Axis]
  Refine = true
  Suppressed = false
  Type = 1
FEATURE [Sketcher::SketchObject] Sketch018
  ArcFitTolerance = 1e-06
  AttachmentSupport = -> [Pocket012]
  ExternalGeometry = -> [Pocket012]
  FullyConstrained = true
  MakeInternals = false
  MapMode = 5
  Placement = pos=(0,-87.5,3.76e-14) rot=(1,0,0;1.5708rad)
  sketch-geometry (2):
    g0: Circle CenterX=66.5 CenterY=-53.5 CenterZ=0 NormalX=0 NormalY=0 NormalZ=1 AngleXU=0 Radius=4.5
    g1: Circle CenterX=63.5 CenterY=62.5 CenterZ=0 NormalX=0 NormalY=0 NormalZ=1 AngleXU=0 Radius=4.5
  constraints (4):
    c: Coincident(g0,g-4)
    c: Coincident(g1,g-3)
    c: Diameter(g1) = 9
    c: Diameter(g0) = 9
FEATURE [PartDesign::Pocket] Pocket013
  BaseFeature = -> Pocket012
  Direction = (0,1,-2e-16)
  Length = 5
  Length2 = 5
  Placement = pos=(0,0,0) rot=(1,0,0;1.5708rad)
  Profile = -> Sketch018
  ReferenceAxis = -> Sketch018 [N_Axis]
  Refine = true
  Suppressed = false
  Type = 0
FEATURE [Sketcher::SketchObject] Sketch019
  ArcFitTolerance = 1e-06
  AttachmentSupport = -> [Pocket013]
  ExternalGeometry = -> [Pocket013]
  FullyConstrained = true
  MakeInternals = false
  MapMode = 5
  Placement = pos=(0,-3e-16,0) rot=(-1,0,0;1.5708rad)
  sketch-geometry (2):
    g0: Circle CenterX=66.5 CenterY=53.5 CenterZ=0 NormalX=0 NormalY=0 NormalZ=1 AngleXU=0 Radius=4.5
    g1: Circle CenterX=63.5 CenterY=-62.5 CenterZ=0 NormalX=0 NormalY=0 NormalZ=1 AngleXU=0 Radius=4.5
  constraints (4):
    c: Coincident(g0,g-3)
    c: Coincident(g1,g-4)
    c: Diameter(g0) = 9
    c: Diameter(g1) = 9
FEATURE [PartDesign::Pocket] Pocket014
  BaseFeature = -> Pocket013
  Direction = (0,-1,-2e-16)
  Length = 5
  Length2 = 5
  Placement = pos=(0,0,0) rot=(1,0,0;1.5708rad)
  Profile = -> Sketch019
  ReferenceAxis = -> Sketch019 [N_Axis]
  Refine = true
  Suppressed = false
  Type = 0
FEATURE [PartDesign::Mirrored] Mirrored
  BaseFeature = -> Pocket014
  MirrorPlane = -> YZ_Plane001
  Placement = pos=(0,0,0) rot=(1,0,0;1.5708rad)
  Refine = true
  Suppressed = false
  TransformMode = 1
FEATURE [PartDesign::Body] Body  label="Stack_Module001"
  AllowCompound = false
  Group = -> [Sketch,Pad,Sketch001,Pocket,Sketch002,Pocket001,Sketch003,Pocket002,Pocket003,Sketch004,Pocket004,LinearPattern,Sketch005,Pad001,Sketch006,Pad002,Fillet,Sketch007,Pad003,Sketch008,Pad004,Sketch009,Pocket005,Sketch010,Pocket006,Fillet001,Fillet002,Sketch011,Pad005,Fillet003,Sketch012,Pocket007,Sketch013,Pocket008,Sketch014,Pocket009,LinearPattern001,Sketch015,Pocket010,Sketch016,Pocket011,+8 more]
  Origin = -> Origin001
  Tip = -> Mirrored
FEATURE [PartDesign::CoordinateSystem] stack_att_up
  AttacherType = Attacher::AttachEngine3D
  AttachmentSupport = -> [Mirrored]
  MapMode = 11
  Placement = pos=(-63.5,-87.5,62.5) rot=(0.57735,0.57735,0.57735;4.18879rad)
FEATURE [PartDesign::CoordinateSystem] stack_att_low
  AttacherType = Attacher::AttachEngine3D
  AttachmentSupport = -> [Mirrored]
  MapMode = 11
  Placement = pos=(-63.5,1.41e-14,62.5) rot=(0.57735,0.57735,-0.57735;2.0944rad)
FEATURE [PartDesign::CoordinateSystem] spacer_att_1
  AttacherType = Attacher::AttachEngine3D
  AttachmentSupport = -> [Mirrored]
  MapMode = 11
  Placement = pos=(66.5,-82.5,-53.5) rot=(0.57735,-0.57735,0.57735;2.0944rad)
FEATURE [PartDesign::CoordinateSystem] spacer_att_2
  AttacherType = Attacher::AttachEngine3D
  AttachmentSupport = -> [Mirrored]
  MapMode = 11
  Placement = pos=(63.5,-82.5,62.5) rot=(0.57735,-0.57735,0.57735;2.0944rad)
FEATURE [PartDesign::CoordinateSystem] spacer_att_3
  AttacherType = Attacher::AttachEngine3D
  AttachmentSupport = -> [Mirrored]
  MapMode = 11
  Placement = pos=(-66.5,-82.5,-53.5) rot=(0.57735,0.57735,0.57735;4.18879rad)
FEATURE [PartDesign::CoordinateSystem] spacer_att_4
  AttacherType = Attacher::AttachEngine3D
  AttachmentSupport = -> [Mirrored]
  MapMode = 11
  Placement = pos=(-63.5,-82.5,62.5) rot=(0.57735,0.57735,0.57735;4.18879rad)
FEATURE [PartDesign::CoordinateSystem] screen_ref  label="screen_reference"
  AttacherType = Attacher::AttachEngine3D
  AttachmentOffset = pos=(4,-50,0) rot=(0,0,1;0rad)
  AttachmentSupport = -> [Mirrored]
  MapMode = 45
  Placement = pos=(-50,-3,-19.9856) rot=(0.57735,0.57735,0.57735;4.18879rad)
FEATURE [App::Part] Part  label="Stack_Module"
  Group = -> [Body,stack_att_up,stack_att_low,spacer_att_1,spacer_att_2,spacer_att_3,spacer_att_4,screen_ref]
  Origin = -> Origin
